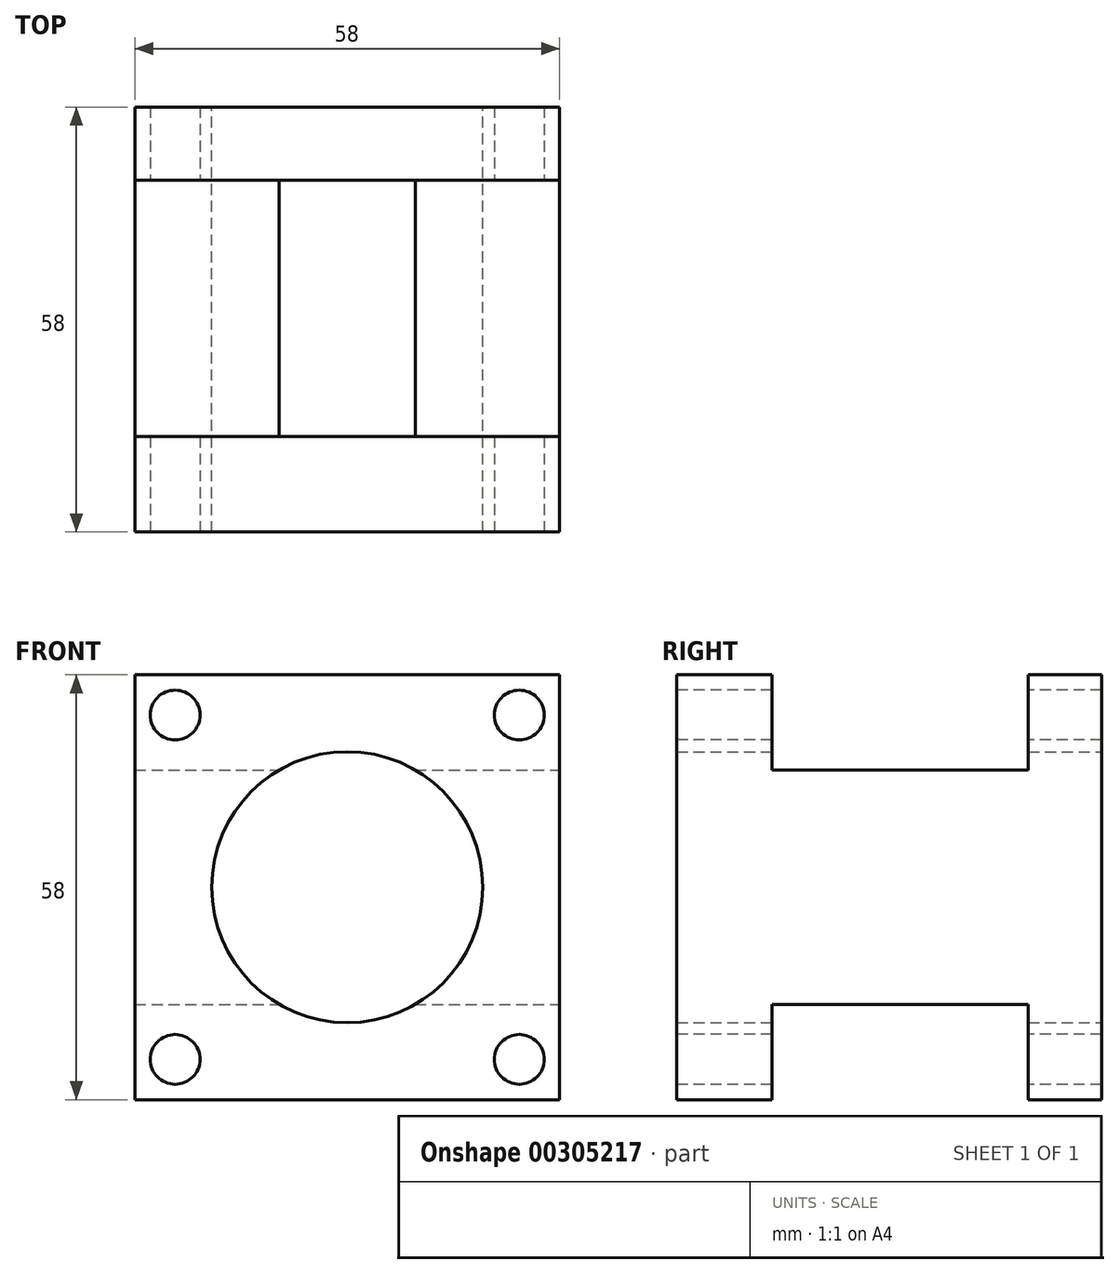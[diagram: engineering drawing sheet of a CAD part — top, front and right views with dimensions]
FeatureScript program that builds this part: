
annotation { "Feature Type Name" : "Feature", "Feature Type Description" : "" }
export const myFeature = defineFeature(function(context is Context, id is Id, definition is map)
    precondition{}
    {
        {
            var Q0;
            Q0=qCreatedBy(makeId("Front.planeOp"),FACE);
            var sketch = newSketch(context, id + "F0", { "sketchPlane" : qUnion([Q0])});
            skLineSegment(sketch, "E0.bottom", {"start": v(0, 0) * mm, "end": v(58, 0) * mm});
            skLineSegment(sketch, "E0.top", {"start": v(0, 58) * mm, "end": v(58, 58) * mm});
            skLineSegment(sketch, "E0.left", {"start": v(0, 0) * mm, "end": v(0, 58) * mm});
            skLineSegment(sketch, "E0.right", {"start": v(58, 0) * mm, "end": v(58, 58) * mm});
            skCircle(sketch, "E1", {"center": v(29, 29) * mm, "radius": 18.5 * mm});
            skSolve(sketch);
        }
        {
            var Q0;
            Q0 = qSketchRegion(id + "F0", true);
            var Q1;
            Q1=makeQuery(id+"F0.imprint","IMPRINT",FACE,{"disambiguationData":[TD([[makeQuery(id+"F0.imprint","IMPRINT",EDGE,{"derivedFrom":sQuery(id+"F0.wireOp",EDGE,"E0.bottom")}),1.0]])]});
            extrude(context, id + "F1", {"entities" : qUnion([Q0, Q1]), "depth" : 58 * mm});
        }
        {
            var Q0;
            Q0=makeQuery(id+"F1.opExtrude","SWEPT_FACE",FACE,{"disambiguationData":[OSD([sQuery(id+"F0.wireOp",EDGE,"E0.top")])]});
            var sketch = newSketch(context, id + "F2", { "sketchPlane" : qUnion([Q0])});
            skLineSegment(sketch, "E2", {"start": v(0, -10) * mm, "end": v(58, -10) * mm});
            skLineSegment(sketch, "E3.0", {"start": v(0, -45) * mm, "end": v(58, -45) * mm});
            skLineSegment(sketch, "E4", {"start": v(0, -45) * mm, "end": v(0, -10) * mm});
            skLineSegment(sketch, "E5", {"start": v(58, -10) * mm, "end": v(58, -45) * mm});
            skSolve(sketch);
        }
        {
            var Q0;
            Q0=makeQuery(id+"F2.imprint","IMPRINT",FACE,{"disambiguationData":[TD([[makeQuery(id+"F2.imprint","IMPRINT",EDGE,{"derivedFrom":sQuery(id+"F2.wireOp",EDGE,"E2")}),-1.0]])]});
            extrude(context, id + "F3", {"entities" : qUnion([Q0]), "operationType" : NewBodyOperationType.REMOVE, "oppositeDirection" : true, "depth" : 13 * mm});
        }
        {
            var Q0;
            Q0=makeQuery(id+"F1.opExtrude","SWEPT_FACE",FACE,{"disambiguationData":[OSD([sQuery(id+"F0.wireOp",EDGE,"E0.bottom")])]});
            var sketch = newSketch(context, id + "F4", { "sketchPlane" : qUnion([Q0])});
            skLineSegment(sketch, "E6", {"start": v(0, 10) * mm, "end": v(58, 10) * mm});
            skLineSegment(sketch, "E7.0", {"start": v(0, 45) * mm, "end": v(58, 45) * mm});
            skLineSegment(sketch, "E8", {"start": v(0, 10) * mm, "end": v(0, 45) * mm});
            skLineSegment(sketch, "E9", {"start": v(58, 10) * mm, "end": v(58, 45) * mm});
            skSolve(sketch);
        }
        {
            var Q0;
            Q0 = qSketchRegion(id + "F4", true);
            var Q1;
            Q1=makeQuery(id+"F4.imprint","IMPRINT",FACE,{"disambiguationData":[TD([[makeQuery(id+"F4.imprint","IMPRINT",EDGE,{"derivedFrom":sQuery(id+"F4.wireOp",EDGE,"E6")}),1.0]])]});
            extrude(context, id + "F5", {"entities" : qUnion([Q0, Q1]), "operationType" : NewBodyOperationType.REMOVE, "oppositeDirection" : true, "depth" : 13 * mm});
        }
        {
            var Q0;
            Q0=makeQuery(id+"F1.opExtrude","CAP_FACE",FACE,{"disambiguationData":[OSD([sQuery(id+"F0.wireOp",EDGE,"E0.bottom"),sQuery(id+"F0.wireOp",EDGE,"E0.top"),sQuery(id+"F0.wireOp",EDGE,"E0.left"),sQuery(id+"F0.wireOp",EDGE,"E0.right"),sQuery(id+"F0.wireOp",EDGE,"E1")])],"isStart":false});
            var sketch = newSketch(context, id + "F6", { "sketchPlane" : qUnion([Q0])});
            skPoint(sketch, "E10", {"position": v(5.5, 52.5) * mm});
            skPoint(sketch, "E11", {"position": v(52.5, 52.5) * mm});
            skPoint(sketch, "E12", {"position": v(52.5, 5.5) * mm});
            skPoint(sketch, "E13", {"position": v(5.5, 5.5) * mm});
            skSolve(sketch);
        }
        {
            var Q0;
            Q0=sQuery(id+"F6.wireOp",VERTEX,"E10");
            var Q1;
            Q1=sQuery(id+"F6.wireOp",VERTEX,"E11");
            var Q2;
            Q2=sQuery(id+"F6.wireOp",VERTEX,"E13");
            var Q3;
            Q3=sQuery(id+"F6.wireOp",VERTEX,"E12");
            var Q4;
            Q4=makeQuery(id+"F1.opExtrude","SWEPT_BODY",BODY,{"disambiguationData":[OSD([sQuery(id+"F0.wireOp",EDGE,"E0.bottom"),sQuery(id+"F0.wireOp",EDGE,"E0.top"),sQuery(id+"F0.wireOp",EDGE,"E0.left"),sQuery(id+"F0.wireOp",EDGE,"E0.right"),sQuery(id+"F0.wireOp",EDGE,"E1")])]});
            hole(context, id + "F7", {"style" : HoleStyle.SIMPLE, "endStyle" : HoleEndStyle.THROUGH, "holeDiameter" : 6.8 * mm, "tappedDepth" : 12 * mm, "tapClearance" : 3, "startFromSketch" : true, "locations" : qUnion([Q0, Q1, Q2, Q3]), "scope" : qUnion([Q4])});
        }
    });
